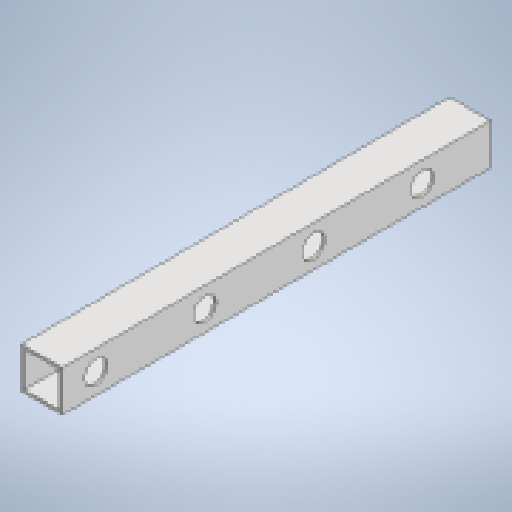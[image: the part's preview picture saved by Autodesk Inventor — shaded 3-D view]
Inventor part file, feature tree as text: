
AUTODESK INVENTOR PART (.ipt)
format: ipt  version: 2025.4 (Build 294407000, 407)  size: 192,512 bytes
history: native  units: mm
features: extrude x2, sketch x2, pattern_linear x1
ambient origin geometry x8: Origin, YZ Plane, XZ Plane, XY Plane, X Axis, Y Axis, Z Axis, Center Point
bodies: Body1 (feature_tree)
feature tree (5):
  extrude  "Extrusion3"  Depth=30.0mm
  extrude  "Extrusion4"  Depth=2.0mm
  pattern_linear  "Rectangular Pattern4"  Count1=32 Spacing1=0.0mm
  sketch  "Sketch9"  dims[d61=320.0mm d172=30.0mm]
  sketch  "Sketch10"  dims[d173=30.0mm d174=2.0mm d175=320.0mm d176=0.0mm d177=17.0mm d178=17.0mm d179=0.0mm d180=0.0mm d181=30.0mm d182=80.0mm d186=17.0mm d187=40.0mm d189=80.0mm]
